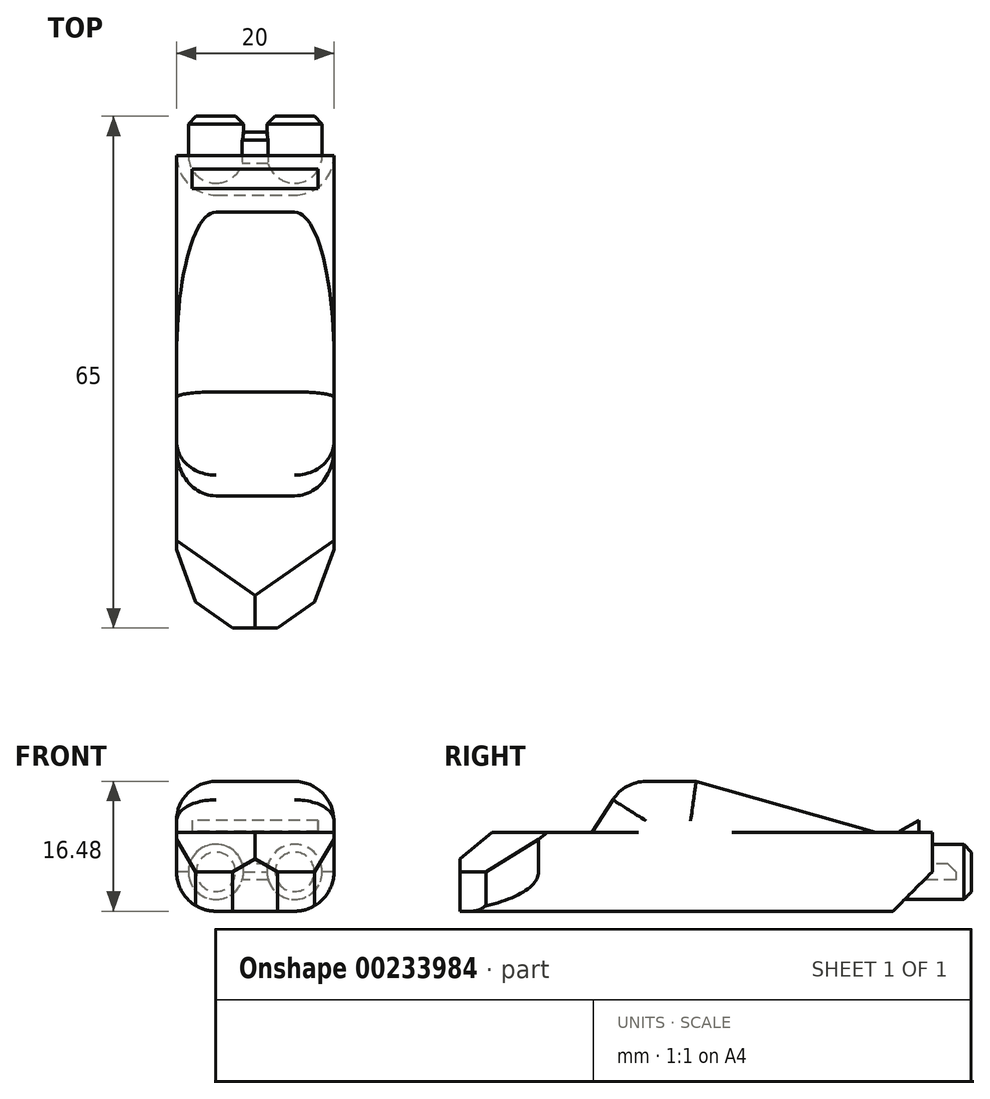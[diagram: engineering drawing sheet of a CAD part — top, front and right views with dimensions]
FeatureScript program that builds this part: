
annotation { "Feature Type Name" : "Feature", "Feature Type Description" : "" }
export const myFeature = defineFeature(function(context is Context, id is Id, definition is map)
    precondition{}
    {
        {
            var Q0;
            Q0=qCreatedBy(makeId("Right.planeOp"),FACE);
            var sketch = newSketch(context, id + "F0", { "sketchPlane" : qUnion([Q0])});
            skLineSegment(sketch, "E0", {"start": v(0, 0) * mm, "end": v(30, 0) * mm});
            skLineSegment(sketch, "E1", {"start": v(0, 0) * mm, "end": v(-30, 0) * mm});
            skLineSegment(sketch, "E2", {"start": v(-30, 0) * mm, "end": v(-30, 5) * mm});
            skLineSegment(sketch, "E3", {"start": v(-30, 5) * mm, "end": v(30, 5) * mm});
            skLineSegment(sketch, "E4", {"start": v(30, 5) * mm, "end": v(30, 0) * mm});
            skLineSegment(sketch, "E5", {"start": v(30, 0) * mm, "end": v(30, -5) * mm});
            skLineSegment(sketch, "E6", {"start": v(30, -5) * mm, "end": v(-30, -5) * mm});
            skLineSegment(sketch, "E7", {"start": v(-30, -5) * mm, "end": v(-30, 0) * mm});
            skLineSegment(sketch, "E8", {"start": v(-13.2, 5) * mm, "end": v(-9.11, 11.48) * mm});
            skLineSegment(sketch, "E9", {"start": v(-9.11, 11.48) * mm, "end": v(0, 11.48) * mm});
            skLineSegment(sketch, "E10", {"start": v(0, 11.48) * mm, "end": v(22.81, 5) * mm});
            skSolve(sketch);
        }
        {
            var Q0;
            Q0=makeQuery(id+"F0.imprint","IMPRINT",FACE,{"disambiguationData":[TD([[makeQuery(id+"F0.imprint","IMPRINT",EDGE,{"derivedFrom":sQuery(id+"F0.wireOp",EDGE,"E0")}),1.0]])]});
            var Q1;
            Q1=makeQuery(id+"F0.imprint","IMPRINT",FACE,{"disambiguationData":[TD([[makeQuery(id+"F0.imprint","IMPRINT",EDGE,{"derivedFrom":sQuery(id+"F0.wireOp",EDGE,"E0")}),-1.0]])]});
            var Q2;
            {var subQ0=sQuery(id+"F0.wireOp",EDGE,"E8");Q2=makeQuery(id+"F0.imprint","IMPRINT",FACE,{"disambiguationData":[TD([[makeQuery(id+"F0.imprint","IMPRINT",EDGE,{"derivedFrom":subQ0}),-1.0]])]});}
            extrude(context, id + "F1", {"entities" : qUnion([Q0, Q1, Q2]), "depth" : 10 * mm});
        }
        {
            var Q0;
            Q0=makeQuery(id+"F1.opExtrude","CAP_FACE",FACE,{"disambiguationData":[OSD([sQuery(id+"F0.wireOp",EDGE,"E2"),sQuery(id+"F0.wireOp",EDGE,"E3"),sQuery(id+"F0.wireOp",EDGE,"E4"),sQuery(id+"F0.wireOp",EDGE,"E5"),sQuery(id+"F0.wireOp",EDGE,"E6"),sQuery(id+"F0.wireOp",EDGE,"E7"),sQuery(id+"F0.wireOp",EDGE,"E8"),sQuery(id+"F0.wireOp",EDGE,"E9"),sQuery(id+"F0.wireOp",EDGE,"E10")])],"isStart":true});
            extrude(context, id + "F2", {"entities" : qUnion([Q0]), "operationType" : NewBodyOperationType.ADD, "depth" : 10 * mm});
        }
        {
            var Q0;
            Q0=makeQuery(id+"F2.opExtrude","CAP_EDGE",EDGE,{"disambiguationData":[OSD([sQuery(id+"F0.wireOp",EDGE,"E2"),sQuery(id+"F0.wireOp",EDGE,"E7")])],"isStart":false});
            var Q1;
            Q1=makeQuery(id+"F1.opExtrude","CAP_EDGE",EDGE,{"disambiguationData":[OSD([sQuery(id+"F0.wireOp",EDGE,"E2"),sQuery(id+"F0.wireOp",EDGE,"E7")])],"isStart":false});
            chamfer(context, id + "F3", {"entities" : qUnion([Q0, Q1]), "chamferType" : ChamferType.OFFSET_ANGLE, "width" : 10 * mm, "oppositeDirection" : false, "angle" : 20 * degree, "tangentPropagation" : true});
        }
        {
            var Q0;
            {var subQ0=sQuery(id+"F0.wireOp",EDGE,"E6");var subQ1=sQuery(id+"F0.wireOp",EDGE,"E5");Q0=makeQuery(id+"F2.boolean.opBoolean","MERGE",EDGE,{"derivedFrom":[makeQuery(id+"F1.opExtrude","SWEPT_EDGE",EDGE,{"disambiguationData":[OSD([subQ1,subQ0])]}),makeQuery(id+"F2.opExtrude","SWEPT_EDGE",EDGE,{"disambiguationData":[OSD([subQ1,subQ0])]})]});}
            chamfer(context, id + "F4", {"entities" : qUnion([Q0]), "width" : 5 * mm, "tangentPropagation" : true});
        }
        {
            var Q0;
            Q0=makeQuery(id+"F2.opExtrude","CAP_EDGE",EDGE,{"disambiguationData":[OSD([sQuery(id+"F0.wireOp",EDGE,"E8")])],"isStart":false});
            var Q1;
            Q1=makeQuery(id+"F1.opExtrude","CAP_EDGE",EDGE,{"disambiguationData":[OSD([sQuery(id+"F0.wireOp",EDGE,"E8")])],"isStart":false});
            var Q2;
            Q2=makeQuery(id+"F2.opExtrude","CAP_EDGE",EDGE,{"disambiguationData":[OSD([sQuery(id+"F0.wireOp",EDGE,"E10")])],"isStart":false});
            var Q3;
            Q3=makeQuery(id+"F1.opExtrude","CAP_EDGE",EDGE,{"disambiguationData":[OSD([sQuery(id+"F0.wireOp",EDGE,"E10")])],"isStart":false});
            var Q4;
            Q4=makeQuery(id+"F2.opExtrude","CAP_EDGE",EDGE,{"disambiguationData":[OSD([sQuery(id+"F0.wireOp",EDGE,"E6")])],"isStart":false});
            var Q5;
            Q5=makeQuery(id+"F1.opExtrude","CAP_EDGE",EDGE,{"disambiguationData":[OSD([sQuery(id+"F0.wireOp",EDGE,"E6")])],"isStart":false});
            fillet(context, id + "F5", {"entities" : qUnion([Q0, Q1, Q2, Q3, Q4, Q5]), "radius" : 5 * mm, "tangentPropagation" : true, "allowEdgeOverflow" : false});
        }
        {
            var Q0;
            {var subQ0=sQuery(id+"F0.wireOp",EDGE,"E7");var subQ1=sQuery(id+"F0.wireOp",EDGE,"E2");Q0=makeQuery(id+"F3.opChamfer","BLEND_EDGE",EDGE,{"blendedFrom":[makeQuery(id+"F1.opExtrude","CAP_EDGE",EDGE,{"disambiguationData":[OSD([subQ1,subQ0])],"isStart":false}),makeQuery(id+"F2.boolean.opBoolean","MERGE",FACE,{"derivedFrom":[makeQuery(id+"F1.opExtrude","SWEPT_FACE",FACE,{"disambiguationData":[OSD([subQ1,subQ0])]}),makeQuery(id+"F2.opExtrude","SWEPT_FACE",FACE,{"disambiguationData":[OSD([subQ1,subQ0])]})]})],"blendedInto":[makeQuery(id+"F2.boolean.opBoolean","MERGE",FACE,{"derivedFrom":[makeQuery(id+"F1.opExtrude","SWEPT_FACE",FACE,{"disambiguationData":[OSD([subQ1,subQ0])]}),makeQuery(id+"F2.opExtrude","SWEPT_FACE",FACE,{"disambiguationData":[OSD([subQ1,subQ0])]})]})]});}
            var Q1;
            {var subQ0=sQuery(id+"F0.wireOp",EDGE,"E7");var subQ1=sQuery(id+"F0.wireOp",EDGE,"E2");Q1=makeQuery(id+"F3.opChamfer","BLEND_EDGE",EDGE,{"blendedFrom":[makeQuery(id+"F2.opExtrude","CAP_EDGE",EDGE,{"disambiguationData":[OSD([subQ1,subQ0])],"isStart":false}),makeQuery(id+"F2.boolean.opBoolean","MERGE",FACE,{"derivedFrom":[makeQuery(id+"F1.opExtrude","SWEPT_FACE",FACE,{"disambiguationData":[OSD([subQ1,subQ0])]}),makeQuery(id+"F2.opExtrude","SWEPT_FACE",FACE,{"disambiguationData":[OSD([subQ1,subQ0])]})]})],"blendedInto":[makeQuery(id+"F2.boolean.opBoolean","MERGE",FACE,{"derivedFrom":[makeQuery(id+"F1.opExtrude","SWEPT_FACE",FACE,{"disambiguationData":[OSD([subQ1,subQ0])]}),makeQuery(id+"F2.opExtrude","SWEPT_FACE",FACE,{"disambiguationData":[OSD([subQ1,subQ0])]})]})]});}
            chamfer(context, id + "F6", {"entities" : qUnion([Q0, Q1]), "width" : 5 * mm, "tangentPropagation" : true});
        }
        {
            var Q0;
            {var subQ0=sQuery(id+"F0.wireOp",EDGE,"E3");var subQ1=sQuery(id+"F0.wireOp",EDGE,"E2");var subQ2=makeQuery(id+"F0.imprint","IMPRINT",EDGE,{"disambiguationData":[TD([[makeQuery(id+"F0.imprint","INTERSECT",VERTEX,{"derivedFrom":[subQ1,subQ0]}),-1.0]])],"derivedFrom":subQ0});var subQ3=sQuery(id+"F0.wireOp",EDGE,"E7");Q0=makeQuery(id+"F6.opChamfer","BLEND_EDGE",EDGE,{"blendedFrom":[makeQuery(id+"F3.opChamfer","BLEND_EDGE",EDGE,{"blendedFrom":[makeQuery(id+"F1.opExtrude","CAP_EDGE",EDGE,{"disambiguationData":[OSD([subQ1,subQ3])],"isStart":false}),makeQuery(id+"F2.boolean.opBoolean","MERGE",FACE,{"derivedFrom":[makeQuery(id+"F1.opExtrude","SWEPT_FACE",FACE,{"disambiguationData":[OSD([subQ1,subQ3])]}),makeQuery(id+"F2.opExtrude","SWEPT_FACE",FACE,{"disambiguationData":[OSD([subQ1,subQ3])]})]})],"blendedInto":[makeQuery(id+"F2.boolean.opBoolean","MERGE",FACE,{"derivedFrom":[makeQuery(id+"F1.opExtrude","SWEPT_FACE",FACE,{"disambiguationData":[OSD([subQ1,subQ3])]}),makeQuery(id+"F2.opExtrude","SWEPT_FACE",FACE,{"disambiguationData":[OSD([subQ1,subQ3])]})]})]}),makeQuery(id+"F2.boolean.opBoolean","MERGE",FACE,{"derivedFrom":[makeQuery(id+"F1.opExtrude","SWEPT_FACE",FACE,{"disambiguationData":[OSD([subQ0]),TDD([subQ2])]}),makeQuery(id+"F2.opExtrude","SWEPT_FACE",FACE,{"disambiguationData":[OSD([subQ0]),TDD([makeQuery(id+"F1.opExtrude","CAP_EDGE",EDGE,{"disambiguationData":[OSD([subQ0]),TDD([subQ2])],"isStart":true})])]})]})],"blendedInto":[makeQuery(id+"F2.boolean.opBoolean","MERGE",FACE,{"derivedFrom":[makeQuery(id+"F1.opExtrude","SWEPT_FACE",FACE,{"disambiguationData":[OSD([subQ0]),TDD([subQ2])]}),makeQuery(id+"F2.opExtrude","SWEPT_FACE",FACE,{"disambiguationData":[OSD([subQ0]),TDD([makeQuery(id+"F1.opExtrude","CAP_EDGE",EDGE,{"disambiguationData":[OSD([subQ0]),TDD([subQ2])],"isStart":true})])]})]})]});}
            var Q1;
            {var subQ0=sQuery(id+"F0.wireOp",EDGE,"E3");var subQ1=sQuery(id+"F0.wireOp",EDGE,"E2");var subQ2=makeQuery(id+"F0.imprint","IMPRINT",EDGE,{"disambiguationData":[TD([[makeQuery(id+"F0.imprint","INTERSECT",VERTEX,{"derivedFrom":[subQ1,subQ0]}),-1.0]])],"derivedFrom":subQ0});var subQ3=sQuery(id+"F0.wireOp",EDGE,"E7");Q1=makeQuery(id+"F6.opChamfer","BLEND_EDGE",EDGE,{"blendedFrom":[makeQuery(id+"F3.opChamfer","BLEND_EDGE",EDGE,{"blendedFrom":[makeQuery(id+"F2.opExtrude","CAP_EDGE",EDGE,{"disambiguationData":[OSD([subQ1,subQ3])],"isStart":false}),makeQuery(id+"F2.boolean.opBoolean","MERGE",FACE,{"derivedFrom":[makeQuery(id+"F1.opExtrude","SWEPT_FACE",FACE,{"disambiguationData":[OSD([subQ1,subQ3])]}),makeQuery(id+"F2.opExtrude","SWEPT_FACE",FACE,{"disambiguationData":[OSD([subQ1,subQ3])]})]})],"blendedInto":[makeQuery(id+"F2.boolean.opBoolean","MERGE",FACE,{"derivedFrom":[makeQuery(id+"F1.opExtrude","SWEPT_FACE",FACE,{"disambiguationData":[OSD([subQ1,subQ3])]}),makeQuery(id+"F2.opExtrude","SWEPT_FACE",FACE,{"disambiguationData":[OSD([subQ1,subQ3])]})]})]}),makeQuery(id+"F2.boolean.opBoolean","MERGE",FACE,{"derivedFrom":[makeQuery(id+"F1.opExtrude","SWEPT_FACE",FACE,{"disambiguationData":[OSD([subQ0]),TDD([subQ2])]}),makeQuery(id+"F2.opExtrude","SWEPT_FACE",FACE,{"disambiguationData":[OSD([subQ0]),TDD([makeQuery(id+"F1.opExtrude","CAP_EDGE",EDGE,{"disambiguationData":[OSD([subQ0]),TDD([subQ2])],"isStart":true})])]})]})],"blendedInto":[makeQuery(id+"F2.boolean.opBoolean","MERGE",FACE,{"derivedFrom":[makeQuery(id+"F1.opExtrude","SWEPT_FACE",FACE,{"disambiguationData":[OSD([subQ0]),TDD([subQ2])]}),makeQuery(id+"F2.opExtrude","SWEPT_FACE",FACE,{"disambiguationData":[OSD([subQ0]),TDD([makeQuery(id+"F1.opExtrude","CAP_EDGE",EDGE,{"disambiguationData":[OSD([subQ0]),TDD([subQ2])],"isStart":true})])]})]})]});}
            chamfer(context, id + "F7", {"entities" : qUnion([Q0, Q1]), "width" : 5 * mm, "tangentPropagation" : true});
        }
        {
            var Q0;
            {var subQ0=sQuery(id+"F0.wireOp",EDGE,"E9");var subQ1=sQuery(id+"F0.wireOp",EDGE,"E8");Q0=makeQuery(id+"F2.boolean.opBoolean","MERGE",EDGE,{"derivedFrom":[makeQuery(id+"F1.opExtrude","SWEPT_EDGE",EDGE,{"disambiguationData":[OSD([subQ1,subQ0])]}),makeQuery(id+"F2.opExtrude","SWEPT_EDGE",EDGE,{"disambiguationData":[OSD([subQ1,subQ0])]})]});}
            fillet(context, id + "F8", {"entities" : qUnion([Q0]), "radius" : 5 * mm, "tangentPropagation" : true, "allowEdgeOverflow" : false});
        }
        {
            var Q0;
            Q0=qCreatedBy(makeId("Front.planeOp"),FACE);
            var sketch = newSketch(context, id + "F9", { "sketchPlane" : qUnion([Q0])});
            skLineSegment(sketch, "E11", {"start": v(0, 0) * mm, "end": v(5, 0) * mm});
            skLineSegment(sketch, "E12", {"start": v(0, 0) * mm, "end": v(-5, 0) * mm});
            skCircle(sketch, "E13", {"center": v(5, 0) * mm, "radius": 3.5 * mm});
            skCircle(sketch, "E14", {"center": v(-5, 0) * mm, "radius": 3.5 * mm});
            skLineSegment(sketch, "E15", {"start": v(5, 0) * mm, "end": v(5, -1) * mm});
            skLineSegment(sketch, "E16", {"start": v(5, -1) * mm, "end": v(-5, -1) * mm});
            skLineSegment(sketch, "E17", {"start": v(-5, -1) * mm, "end": v(-5, 1) * mm});
            skLineSegment(sketch, "E18", {"start": v(-5, 1) * mm, "end": v(5, 1) * mm});
            skLineSegment(sketch, "E19", {"start": v(5, 1) * mm, "end": v(5, 0) * mm});
            skSolve(sketch);
        }
        {
            var Q0;
            {var subQ1=sQuery(id+"F9.wireOp",EDGE,"E15");Q0=makeQuery(id+"F9.imprint","IMPRINT",FACE,{"disambiguationData":[TD([[makeQuery(id+"F9.imprint","IMPRINT",EDGE,{"derivedFrom":subQ1}),1.0]])]});}
            var Q1;
            {var subQ0=sQuery(id+"F9.wireOp",EDGE,"E17");var subQ1=sQuery(id+"F9.wireOp",EDGE,"E12");var subQ2=makeQuery(id+"F9.imprint","INTERSECT",VERTEX,{"derivedFrom":[subQ1,subQ0]});Q1=makeQuery(id+"F9.imprint","IMPRINT",FACE,{"disambiguationData":[TD([[makeQuery(id+"F9.imprint","IMPRINT",EDGE,{"disambiguationData":[TD([[subQ2,1.0]])],"derivedFrom":subQ1}),1.0]])]});}
            var Q2;
            {var subQ0=sQuery(id+"F9.wireOp",EDGE,"E17");var subQ1=sQuery(id+"F9.wireOp",EDGE,"E12");var subQ2=makeQuery(id+"F9.imprint","INTERSECT",VERTEX,{"derivedFrom":[subQ1,subQ0]});Q2=makeQuery(id+"F9.imprint","IMPRINT",FACE,{"disambiguationData":[TD([[makeQuery(id+"F9.imprint","IMPRINT",EDGE,{"disambiguationData":[TD([[subQ2,1.0]])],"derivedFrom":subQ1}),-1.0]])]});}
            var Q3;
            {var subQ0=sQuery(id+"F9.wireOp",EDGE,"E19");Q3=makeQuery(id+"F9.imprint","IMPRINT",FACE,{"disambiguationData":[TD([[makeQuery(id+"F9.imprint","IMPRINT",EDGE,{"derivedFrom":subQ0}),-1.0]])]});}
            var Q4;
            {var subQ0=sQuery(id+"F9.wireOp",EDGE,"E15");Q4=makeQuery(id+"F9.imprint","IMPRINT",FACE,{"disambiguationData":[TD([[makeQuery(id+"F9.imprint","IMPRINT",EDGE,{"derivedFrom":subQ0}),-1.0]])]});}
            var Q5;
            {var subQ2=sQuery(id+"F9.wireOp",EDGE,"E18");var subQ6=sQuery(id+"F9.wireOp",EDGE,"E14");var subQ8=makeQuery(id+"F9.imprint","INTERSECT",VERTEX,{"derivedFrom":[subQ6,subQ2]});Q5=makeQuery(id+"F9.imprint","IMPRINT",FACE,{"disambiguationData":[TD([[makeQuery(id+"F9.imprint","IMPRINT",EDGE,{"disambiguationData":[TD([[subQ8,-1.0]])],"derivedFrom":subQ6}),1.0]])]});}
            extrude(context, id + "F10", {"entities" : qUnion([Q0, Q1, Q2, Q3, Q4, Q5]), "operationType" : NewBodyOperationType.ADD, "oppositeDirection" : true, "depth" : 35 * mm});
        }
        {
            var Q0;
            {var subQ3=sQuery(id+"F9.wireOp",EDGE,"E11");var subQ5=sQuery(id+"F9.wireOp",EDGE,"E12");var subQ6=makeQuery(id+"F9.imprint","INTERSECT",VERTEX,{"derivedFrom":[subQ3,subQ5]});Q0=makeQuery(id+"F9.imprint","IMPRINT",FACE,{"disambiguationData":[TD([[makeQuery(id+"F9.imprint","IMPRINT",EDGE,{"disambiguationData":[TD([[subQ6,-1.0]])],"derivedFrom":subQ3}),-1.0]])]});}
            var Q1;
            {var subQ3=sQuery(id+"F9.wireOp",EDGE,"E12");var subQ5=sQuery(id+"F9.wireOp",EDGE,"E11");var subQ6=makeQuery(id+"F9.imprint","INTERSECT",VERTEX,{"derivedFrom":[subQ5,subQ3]});Q1=makeQuery(id+"F9.imprint","IMPRINT",FACE,{"disambiguationData":[TD([[makeQuery(id+"F9.imprint","IMPRINT",EDGE,{"disambiguationData":[TD([[subQ6,-1.0]])],"derivedFrom":subQ5}),1.0]])]});}
            extrude(context, id + "F11", {"entities" : qUnion([Q0, Q1]), "operationType" : NewBodyOperationType.ADD, "oppositeDirection" : true, "depth" : 33 * mm});
        }
        {
            var Q0;
            Q0=makeQuery(id+"F10.opExtrude","CAP_EDGE",EDGE,{"disambiguationData":[OSD([sQuery(id+"F9.wireOp",EDGE,"E13")])],"isStart":false});
            var Q1;
            Q1=makeQuery(id+"F10.opExtrude","CAP_EDGE",EDGE,{"disambiguationData":[OSD([sQuery(id+"F9.wireOp",EDGE,"E14")])],"isStart":false});
            var Q2;
            Q2=makeQuery(id+"F11.opExtrude","CAP_EDGE",EDGE,{"disambiguationData":[OSD([sQuery(id+"F9.wireOp",EDGE,"E18")])],"isStart":false});
            chamfer(context, id + "F12", {"entities" : qUnion([Q0, Q1, Q2]), "width" : 1 * mm, "tangentPropagation" : true});
        }
        {
            var Q0;
            {var subQ0=sQuery(id+"F0.wireOp",EDGE,"E3");var subQ1=makeQuery(id+"F0.imprint","IMPRINT",EDGE,{"disambiguationData":[TD([[makeQuery(id+"F0.imprint","INTERSECT",VERTEX,{"derivedFrom":[subQ0,sQuery(id+"F0.wireOp",EDGE,"E4")]}),1.0]])],"derivedFrom":subQ0});Q0=makeQuery(id+"F2.boolean.opBoolean","MERGE",FACE,{"derivedFrom":[makeQuery(id+"F1.opExtrude","SWEPT_FACE",FACE,{"disambiguationData":[OSD([subQ0]),TDD([subQ1])]}),makeQuery(id+"F2.opExtrude","SWEPT_FACE",FACE,{"disambiguationData":[OSD([subQ0]),TDD([makeQuery(id+"F1.opExtrude","CAP_EDGE",EDGE,{"disambiguationData":[OSD([subQ0]),TDD([subQ1])],"isStart":true})])]})]});}
            var sketch = newSketch(context, id + "F13", { "sketchPlane" : qUnion([Q0])});
            skLineSegment(sketch, "E20", {"start": v(0, 22.81) * mm, "end": v(0, 25.81) * mm});
            skPoint(sketch, "E20.endSnap0", {"position": v(0, 22.81) * mm});
            skLineSegment(sketch, "E21", {"start": v(0, 25.81) * mm, "end": v(-8, 25.81) * mm});
            skLineSegment(sketch, "E22", {"start": v(-8, 25.81) * mm, "end": v(-8, 28.31) * mm});
            skLineSegment(sketch, "E23", {"start": v(-8, 28.31) * mm, "end": v(8, 28.31) * mm});
            skLineSegment(sketch, "E24", {"start": v(8, 28.31) * mm, "end": v(8, 25.81) * mm});
            skLineSegment(sketch, "E25", {"start": v(8, 25.81) * mm, "end": v(0, 25.81) * mm});
            skSolve(sketch);
        }
        {
            var Q0;
            Q0=makeQuery(id+"F13.imprint","IMPRINT",FACE,{"disambiguationData":[TD([[makeQuery(id+"F13.imprint","IMPRINT",EDGE,{"derivedFrom":sQuery(id+"F13.wireOp",EDGE,"E21")}),-1.0]])]});
            extrude(context, id + "F14", {"entities" : qUnion([Q0]), "operationType" : NewBodyOperationType.ADD, "depth" : 3 * mm});
        }
        {
            var Q0;
            Q0=makeQuery(id+"F14.opExtrude","CAP_EDGE",EDGE,{"disambiguationData":[OSD([sQuery(id+"F13.wireOp",EDGE,"E21"),sQuery(id+"F13.wireOp",EDGE,"E25")])],"isStart":false});
            chamfer(context, id + "F15", {"entities" : qUnion([Q0]), "chamferType" : ChamferType.OFFSET_ANGLE, "width" : 5 * mm, "oppositeDirection" : true, "angle" : 30 * degree, "tangentPropagation" : true});
        }
    });
